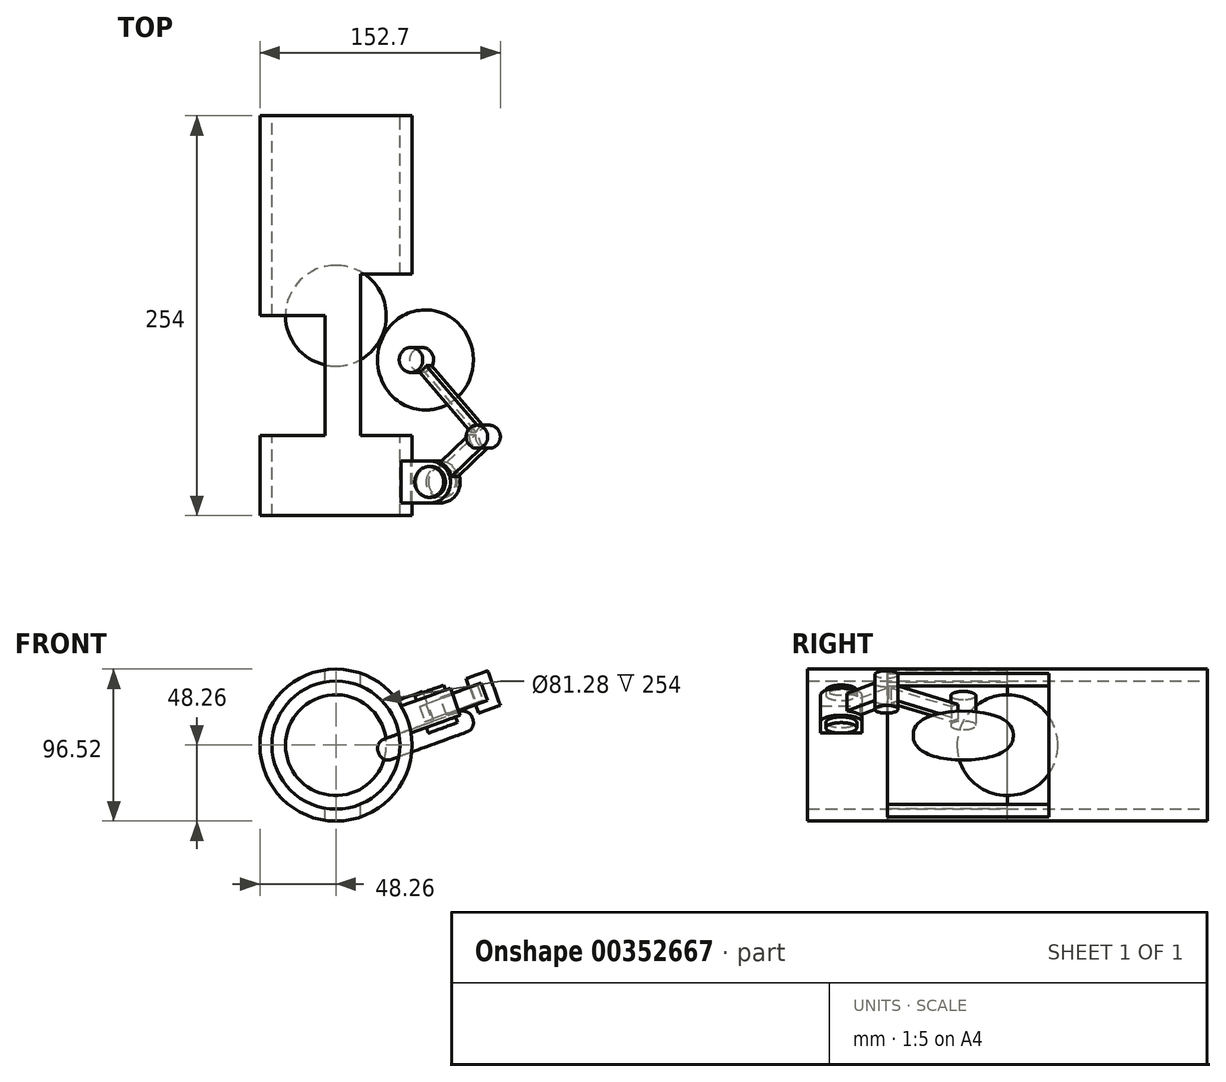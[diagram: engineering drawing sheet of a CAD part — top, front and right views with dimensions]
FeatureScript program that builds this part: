
annotation { "Feature Type Name" : "Feature", "Feature Type Description" : "" }
export const myFeature = defineFeature(function(context is Context, id is Id, definition is map)
    precondition{}
    {
        {
            var Q0;
            Q0=qCreatedBy(makeId("Front.planeOp"),FACE);
            var sketch = newSketch(context, id + "F0", { "sketchPlane" : qUnion([Q0])});
            skCircle(sketch, "E0", {"center": v(0, 0) * mm, "radius": 40.64 * mm});
            skCircle(sketch, "E1", {"center": v(0, 0) * mm, "radius": 48.26 * mm});
            skSolve(sketch);
        }
        {
            var Q0;
            Q0 = qSketchRegion(id + "F0", true);
            extrude(context, id + "F1", {"entities" : qUnion([Q0]), "endBound" : BoundingType.SYMMETRIC, "depth" : 254 * mm});
        }
        {
            var Q0;
            Q0=qCreatedBy(makeId("Top.planeOp"),FACE);
            var sketch = newSketch(context, id + "F2", { "sketchPlane" : qUnion([Q0])});
            skLineSegment(sketch, "E2", {"start": v(-7.03, 0) * mm, "end": v(-50.8, 0) * mm});
            skLineSegment(sketch, "E3", {"start": v(-50.8, 0) * mm, "end": v(-50.8, -76.2) * mm});
            skLineSegment(sketch, "E4", {"start": v(-50.8, -76.2) * mm, "end": v(-7.03, -76.2) * mm});
            skLineSegment(sketch, "E5", {"start": v(-7.03, -76.2) * mm, "end": v(-7.03, 0) * mm});
            skLineSegment(sketch, "E6", {"start": v(50.8, 0) * mm, "end": v(50.8, 26.36) * mm});
            skLineSegment(sketch, "E7", {"start": v(50.8, 26.36) * mm, "end": v(15.72, 26.36) * mm});
            skLineSegment(sketch, "E8", {"start": v(15.72, 26.36) * mm, "end": v(15.72, -76.2) * mm});
            skLineSegment(sketch, "E9", {"start": v(15.72, -76.2) * mm, "end": v(50.8, -76.2) * mm});
            skLineSegment(sketch, "E10", {"start": v(50.8, 0) * mm, "end": v(50.8, -76.2) * mm});
            skSolve(sketch);
        }
        {
            var Q0;
            Q0 = qSketchRegion(id + "F2", true);
            extrude(context, id + "F3", {"entities" : qUnion([Q0]), "operationType" : NewBodyOperationType.REMOVE, "endBound" : BoundingType.SYMMETRIC, "oppositeDirection" : true, "depth" : 144.27 * mm});
        }
        {
            var Q0;
            Q0=makeQuery(id+"F1.opExtrude","SWEPT_FACE",FACE,{"disambiguationData":[OSD([sQuery(id+"F0.wireOp",EDGE,"E1")])]});
            cPlane(context, id + "F4", {"entities" : qUnion([Q0]), "cplaneType" : CPlaneType.LINE_ANGLE, "offset" : 25.4 * mm, "angle" : 160 * degree, "width" : 152.4 * mm, "height" : 152.4 * mm});
        }
        {
            var Q0;
            Q0=qCreatedBy(id+"F4.planeOp",FACE);
            var sketch = newSketch(context, id + "F5", { "sketchPlane" : qUnion([Q0])});
            skLineSegment(sketch, "E11", {"start": v(0, 0) * mm, "end": v(44.45, 0) * mm});
            skLineSegment(sketch, "E12", {"start": v(44.45, 92.42) * mm, "end": v(44.45, 118.85) * mm});
            skLineSegment(sketch, "E13", {"start": v(44.45, 118.85) * mm, "end": v(67.52, 118.85) * mm});
            skLineSegment(sketch, "E14", {"start": v(67.52, 92.42) * mm, "end": v(44.45, 92.42) * mm});
            skArc(sketch, "E15", {"start": v(67.52, 92.42) * mm, "mid": v(80.74, 105.63) * mm, "end": v(67.52, 118.85) * mm});
            skSolve(sketch);
        }
        {
            var Q0;
            Q0 = qSketchRegion(id + "F5", true);
            extrude(context, id + "F6", {"entities" : qUnion([Q0]), "operationType" : NewBodyOperationType.ADD, "endBound" : BoundingType.SYMMETRIC, "depth" : 18.29 * mm});
        }
        {
            var Q0;
            Q0=makeQuery(id+"F6.opExtrude","CAP_FACE",FACE,{"disambiguationData":[OSD([sQuery(id+"F5.wireOp",EDGE,"E12"),sQuery(id+"F5.wireOp",EDGE,"E13"),sQuery(id+"F5.wireOp",EDGE,"E14"),sQuery(id+"F5.wireOp",EDGE,"E15")])],"isStart":true});
            cPlane(context, id + "F7", {"entities" : qUnion([Q0]), "cplaneType" : CPlaneType.OFFSET, "offset" : 9.4 * mm, "oppositeDirection" : true, "width" : 152.4 * mm, "height" : 152.4 * mm});
        }
        {
            var Q0;
            Q0=qCreatedBy(id+"F7.planeOp",FACE);
            var sketch = newSketch(context, id + "F8", { "sketchPlane" : qUnion([Q0])});
            skCircle(sketch, "E16", {"center": v(67.63, -105.55) * mm, "radius": 9.8 * mm});
            skCircle(sketch, "E17", {"center": v(99.5, -76.85) * mm, "radius": 7.3 * mm});
            skCircle(sketch, "E18", {"center": v(55.57, -28.09) * mm, "radius": 7.96 * mm});
            skLineSegment(sketch, "E19", {"start": v(69.57, -95.96) * mm, "end": v(92.32, -75.46) * mm});
            skLineSegment(sketch, "E20", {"start": v(77.38, -104.63) * mm, "end": v(100.13, -84.13) * mm});
            skLineSegment(sketch, "E21", {"start": v(92.77, -73.98) * mm, "end": v(58.2, -35.6) * mm});
            skLineSegment(sketch, "E22", {"start": v(97.35, -69.87) * mm, "end": v(62.77, -31.49) * mm});
            skSolve(sketch);
        }
        {
            var Q0;
            {var subQ0=sQuery(id+"F8.wireOp",EDGE,"E16");var subQ1=makeQuery(id+"F8.imprint","INTERSECT",VERTEX,{"derivedFrom":[subQ0,sQuery(id+"F8.wireOp",EDGE,"E19")]});Q0=makeQuery(id+"F8.imprint","IMPRINT",FACE,{"disambiguationData":[TD([[makeQuery(id+"F8.imprint","IMPRINT",EDGE,{"disambiguationData":[TD([[subQ1,1.0]])],"derivedFrom":subQ0}),1.0]])]});}
            extrude(context, id + "F9", {"entities" : qUnion([Q0]), "operationType" : NewBodyOperationType.ADD, "endBound" : BoundingType.SYMMETRIC, "depth" : 25.4 * mm});
        }
        {
            var Q0;
            {var subQ0=sQuery(id+"F8.wireOp",EDGE,"E19");Q0=makeQuery(id+"F8.imprint","IMPRINT",FACE,{"disambiguationData":[TD([[makeQuery(id+"F8.imprint","IMPRINT",EDGE,{"derivedFrom":subQ0}),-1.0]])]});}
            extrude(context, id + "F10", {"entities" : qUnion([Q0]), "operationType" : NewBodyOperationType.ADD, "endBound" : BoundingType.SYMMETRIC, "depth" : 11.68 * mm});
        }
        {
            var Q0;
            {var subQ0=sQuery(id+"F8.wireOp",EDGE,"E17");var subQ1=makeQuery(id+"F8.imprint","INTERSECT",VERTEX,{"derivedFrom":[subQ0,sQuery(id+"F8.wireOp",EDGE,"E21")]});Q0=makeQuery(id+"F8.imprint","IMPRINT",FACE,{"disambiguationData":[TD([[makeQuery(id+"F8.imprint","IMPRINT",EDGE,{"disambiguationData":[TD([[subQ1,1.0]])],"derivedFrom":subQ0}),1.0]])]});}
            extrude(context, id + "F11", {"entities" : qUnion([Q0]), "operationType" : NewBodyOperationType.ADD, "endBound" : BoundingType.SYMMETRIC, "depth" : 23.37 * mm});
        }
        {
            var Q0;
            {var subQ0=sQuery(id+"F8.wireOp",EDGE,"E21");Q0=makeQuery(id+"F8.imprint","IMPRINT",FACE,{"disambiguationData":[TD([[makeQuery(id+"F8.imprint","IMPRINT",EDGE,{"derivedFrom":subQ0}),-1.0]])]});}
            extrude(context, id + "F12", {"entities" : qUnion([Q0]), "operationType" : NewBodyOperationType.ADD, "endBound" : BoundingType.SYMMETRIC, "depth" : 10.16 * mm});
        }
        {
            var Q0;
            {var subQ0=sQuery(id+"F8.wireOp",EDGE,"E18");var subQ1=makeQuery(id+"F8.imprint","INTERSECT",VERTEX,{"derivedFrom":[subQ0,sQuery(id+"F8.wireOp",EDGE,"E21")]});Q0=makeQuery(id+"F8.imprint","IMPRINT",FACE,{"disambiguationData":[TD([[makeQuery(id+"F8.imprint","IMPRINT",EDGE,{"disambiguationData":[TD([[subQ1,-1.0]])],"derivedFrom":subQ0}),1.0]])]});}
            extrude(context, id + "F13", {"entities" : qUnion([Q0]), "operationType" : NewBodyOperationType.ADD, "endBound" : BoundingType.SYMMETRIC, "depth" : 26.92 * mm});
        }
        {
            var Q0;
            Q0=makeQuery(id+"F13.opExtrude","CAP_FACE",FACE,{"disambiguationData":[OSD([sQuery(id+"F8.wireOp",EDGE,"E18")])],"isStart":true});
            var sketch = newSketch(context, id + "F14", { "sketchPlane" : qUnion([Q0])});
            skCircle(sketch, "E23", {"center": v(55.57, 28.09) * mm, "radius": 31.75 * mm});
            skSolve(sketch);
        }
        {
            var Q0;
            Q0=makeQuery(id+"F14.imprint","IMPRINT",FACE,{"disambiguationData":[TD([[makeQuery(id+"F14.imprint","IMPRINT",EDGE,{"derivedFrom":sQuery(id+"F14.wireOp",EDGE,"E23")}),1.0]])]});
            var Q1;
            Q1=makeQuery(id+"F14.imprint","IMPRINT",FACE,{"disambiguationData":[TD([[makeQuery(id+"F14.imprint","IMPRINT",EDGE,{"derivedFrom":makeQuery(id+"F13.opExtrude","CAP_EDGE",EDGE,{"disambiguationData":[OSD([sQuery(id+"F8.wireOp",EDGE,"E18")])],"isStart":true})}),-1.0]])]});
            extrude(context, id + "F15", {"entities" : qUnion([Q0, Q1]), "operationType" : NewBodyOperationType.ADD, "endBound" : BoundingType.SYMMETRIC, "depth" : 13.72 * mm});
        }
        {
            var Q0;
            Q0=makeQuery(id+"F15.opExtrude","SWEPT_FACE",FACE,{"disambiguationData":[OSD([sQuery(id+"F14.wireOp",EDGE,"E23")])]});
            fillet(context, id + "F16", {"entities" : qUnion([Q0]), "radius" : 6.13 * mm, "tangentPropagation" : true, "allowEdgeOverflow" : false});
        }
        {
            var Q0;
            Q0=qCreatedBy(makeId("Top.planeOp"),FACE);
            var sketch = newSketch(context, id + "F17", { "sketchPlane" : qUnion([Q0])});
            skArc(sketch, "E24", {"start": v(0, -32) * mm, "mid": v(32, 0) * mm, "end": v(0, 32) * mm});
            skLineSegment(sketch, "E25", {"start": v(0, 0) * mm, "end": v(0, -37.08) * mm});
            skLineSegment(sketch, "E26", {"start": v(0, 0) * mm, "end": v(0, 33.37) * mm});
            skSolve(sketch);
        }
        {
            var Q0;
            Q0 = qSketchRegion(id + "F17", true);
            var Q1;
            Q1=sQuery(id+"F17.wireOp",EDGE,"E25");
            revolve(context, id + "F18", {"operationType" : NewBodyOperationType.ADD, "entities" : qUnion([Q0]), "axis" : qUnion([Q1]), "revolveType" : RevolveType.FULL});
        }
    });
